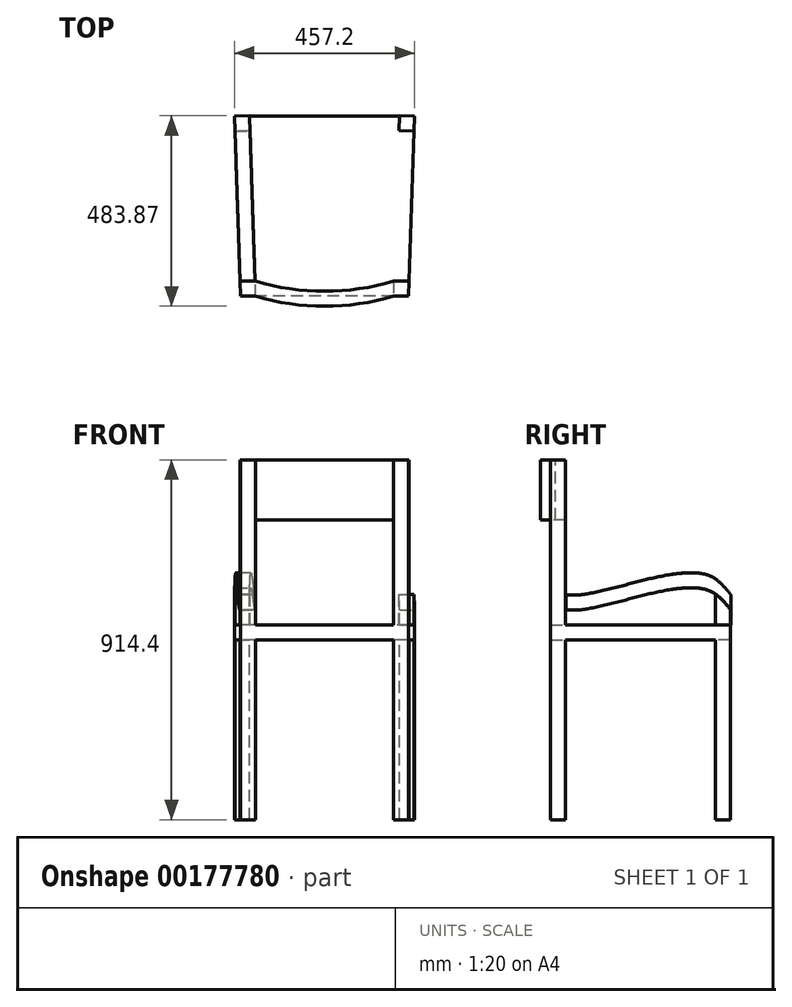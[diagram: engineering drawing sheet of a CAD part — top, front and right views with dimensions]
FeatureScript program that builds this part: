
annotation { "Feature Type Name" : "Feature", "Feature Type Description" : "" }
export const myFeature = defineFeature(function(context is Context, id is Id, definition is map)
    precondition{}
    {
        {
            var Q0;
            Q0=qCreatedBy(makeId("Top.planeOp"),FACE);
            var sketch = newSketch(context, id + "F0", { "sketchPlane" : qUnion([Q0])});
            skLineSegment(sketch, "E0", {"start": v(0, 0) * mm, "end": v(0, 228.6) * mm});
            skLineSegment(sketch, "E1", {"start": v(0, 0) * mm, "end": v(0, -228.6) * mm});
            skLineSegment(sketch, "E2", {"start": v(0, 228.6) * mm, "end": v(228.6, 228.6) * mm});
            skLineSegment(sketch, "E3", {"start": v(0, 228.6) * mm, "end": v(-228.6, 228.6) * mm});
            skLineSegment(sketch, "E4", {"start": v(0, -228.6) * mm, "end": v(-213.36, -228.6) * mm});
            skLineSegment(sketch, "E5", {"start": v(0, -228.6) * mm, "end": v(213.36, -228.6) * mm});
            skLineSegment(sketch, "E6", {"start": v(-228.6, 228.6) * mm, "end": v(-213.36, -228.6) * mm});
            skLineSegment(sketch, "E7", {"start": v(228.6, 228.6) * mm, "end": v(213.36, -228.6) * mm});
            skSolve(sketch);
        }
        {
            var Q0;
            Q0=makeQuery(id+"F0.imprint","IMPRINT",FACE,{"disambiguationData":[TD([[makeQuery(id+"F0.imprint","IMPRINT",EDGE,{"derivedFrom":sQuery(id+"F0.wireOp",EDGE,"E0")}),1.0]])]});
            var Q1;
            Q1=makeQuery(id+"F0.imprint","IMPRINT",FACE,{"disambiguationData":[TD([[makeQuery(id+"F0.imprint","IMPRINT",EDGE,{"derivedFrom":sQuery(id+"F0.wireOp",EDGE,"E0")}),-1.0]])]});
            extrude(context, id + "F1", {"entities" : qUnion([Q0, Q1]), "depth" : 38.1 * mm});
        }
        {
            var Q0;
            Q0=makeQuery(id+"F1.opExtrude","CAP_FACE",FACE,{"disambiguationData":[OSD([sQuery(id+"F0.wireOp",EDGE,"E2"),sQuery(id+"F0.wireOp",EDGE,"E3"),sQuery(id+"F0.wireOp",EDGE,"E4"),sQuery(id+"F0.wireOp",EDGE,"E5"),sQuery(id+"F0.wireOp",EDGE,"E6"),sQuery(id+"F0.wireOp",EDGE,"E7")])],"isStart":true});
            var sketch = newSketch(context, id + "F2", { "sketchPlane" : qUnion([Q0])});
            skLineSegment(sketch, "E8.bottom", {"start": v(228.6, -228.6) * mm, "end": v(190.5, -228.6) * mm});
            skLineSegment(sketch, "E8.top", {"start": v(228.6, -190.5) * mm, "end": v(190.5, -190.5) * mm});
            skLineSegment(sketch, "E8.left", {"start": v(228.6, -228.6) * mm, "end": v(228.6, -190.5) * mm});
            skLineSegment(sketch, "E8.right", {"start": v(190.5, -228.6) * mm, "end": v(190.5, -190.5) * mm});
            skLineSegment(sketch, "E9.bottom", {"start": v(-228.6, -228.6) * mm, "end": v(-190.5, -228.6) * mm});
            skLineSegment(sketch, "E9.top", {"start": v(-228.6, -190.5) * mm, "end": v(-190.5, -190.5) * mm});
            skLineSegment(sketch, "E9.left", {"start": v(-228.6, -228.6) * mm, "end": v(-228.6, -190.5) * mm});
            skLineSegment(sketch, "E9.right", {"start": v(-190.5, -228.6) * mm, "end": v(-190.5, -190.5) * mm});
            skSolve(sketch);
        }
        {
            var Q0;
            {var subQ0=sQuery(id+"F2.wireOp",EDGE,"E8.bottom");Q0=makeQuery(id+"F2.imprint","IMPRINT",FACE,{"disambiguationData":[TD([[makeQuery(id+"F2.imprint","IMPRINT",EDGE,{"derivedFrom":subQ0}),-1.0]])]});}
            var Q1;
            {var subQ0=sQuery(id+"F2.wireOp",EDGE,"E9.bottom");Q1=makeQuery(id+"F2.imprint","IMPRINT",FACE,{"disambiguationData":[TD([[makeQuery(id+"F2.imprint","IMPRINT",EDGE,{"derivedFrom":subQ0}),-1.0]])]});}
            extrude(context, id + "F3", {"entities" : qUnion([Q0, Q1]), "operationType" : NewBodyOperationType.ADD, "depth" : 457.2 * mm});
        }
        {
            var Q0;
            Q0=makeQuery(id+"F1.opExtrude","CAP_FACE",FACE,{"disambiguationData":[OSD([sQuery(id+"F0.wireOp",EDGE,"E2"),sQuery(id+"F0.wireOp",EDGE,"E3"),sQuery(id+"F0.wireOp",EDGE,"E4"),sQuery(id+"F0.wireOp",EDGE,"E5"),sQuery(id+"F0.wireOp",EDGE,"E6"),sQuery(id+"F0.wireOp",EDGE,"E7")])],"isStart":true});
            var sketch = newSketch(context, id + "F4", { "sketchPlane" : qUnion([Q0])});
            skLineSegment(sketch, "E10.bottom", {"start": v(-213.36, 228.6) * mm, "end": v(-175.26, 228.6) * mm});
            skLineSegment(sketch, "E10.top", {"start": v(-213.36, 190.5) * mm, "end": v(-175.26, 190.5) * mm});
            skLineSegment(sketch, "E10.left", {"start": v(-213.36, 228.6) * mm, "end": v(-213.36, 190.5) * mm});
            skLineSegment(sketch, "E10.right", {"start": v(-175.26, 228.6) * mm, "end": v(-175.26, 190.5) * mm});
            skLineSegment(sketch, "E11.bottom", {"start": v(213.36, 228.6) * mm, "end": v(175.26, 228.6) * mm});
            skLineSegment(sketch, "E11.top", {"start": v(213.36, 190.5) * mm, "end": v(175.26, 190.5) * mm});
            skLineSegment(sketch, "E11.left", {"start": v(213.36, 228.6) * mm, "end": v(213.36, 190.5) * mm});
            skLineSegment(sketch, "E11.right", {"start": v(175.26, 228.6) * mm, "end": v(175.26, 190.5) * mm});
            skLineSegment(sketch, "E12", {"start": v(-213.36, 190.5) * mm, "end": v(-214.63, 190.5) * mm});
            skLineSegment(sketch, "E13", {"start": v(213.36, 190.5) * mm, "end": v(214.63, 190.5) * mm});
            skSolve(sketch);
        }
        {
            var Q0;
            {var subQ0=sQuery(id+"F4.wireOp",EDGE,"E10.left");Q0=makeQuery(id+"F4.imprint","IMPRINT",FACE,{"disambiguationData":[TD([[makeQuery(id+"F4.imprint","IMPRINT",EDGE,{"derivedFrom":subQ0}),-1.0]])]});}
            var Q1;
            Q1=makeQuery(id+"F4.imprint","IMPRINT",FACE,{"disambiguationData":[TD([[makeQuery(id+"F4.imprint","IMPRINT",EDGE,{"derivedFrom":sQuery(id+"F4.wireOp",EDGE,"E10.bottom")}),1.0]])]});
            var Q2;
            Q2=makeQuery(id+"F4.imprint","IMPRINT",FACE,{"disambiguationData":[TD([[makeQuery(id+"F4.imprint","IMPRINT",EDGE,{"derivedFrom":sQuery(id+"F4.wireOp",EDGE,"E11.bottom")}),1.0]])]});
            var Q3;
            {var subQ0=sQuery(id+"F4.wireOp",EDGE,"E11.left");Q3=makeQuery(id+"F4.imprint","IMPRINT",FACE,{"disambiguationData":[TD([[makeQuery(id+"F4.imprint","IMPRINT",EDGE,{"derivedFrom":subQ0}),1.0]])]});}
            extrude(context, id + "F5", {"entities" : qUnion([Q0, Q1, Q2, Q3]), "operationType" : NewBodyOperationType.ADD, "endBound" : BoundingType.SYMMETRIC, "depth" : 914.4 * mm});
        }
        {
            var Q0;
            {var subQ0=sQuery(id+"F0.wireOp",EDGE,"E7");Q0=makeQuery(id+"F5.boolean.opBoolean","MERGE",FACE,{"derivedFrom":[makeQuery(id+"F3.boolean.opBoolean","MERGE",FACE,{"derivedFrom":[makeQuery(id+"F1.opExtrude","SWEPT_FACE",FACE,{"disambiguationData":[OSD([subQ0])]}),makeQuery(id+"F3.opExtrude","SWEPT_FACE",FACE,{"disambiguationData":[OSD([subQ0])]})]}),makeQuery(id+"F5.opExtrude","SWEPT_FACE",FACE,{"disambiguationData":[OSD([subQ0])]})]});}
            var sketch = newSketch(context, id + "F6", { "sketchPlane" : qUnion([Q0])});
            skLineSegment(sketch, "E14", {"start": v(236.09, 38.1) * mm, "end": v(236.09, 114.3) * mm});
            skFitSpline(sketch, "E15", {"points": [v(236.09, 114.3) * mm, v(177.93, 164.06) * mm, v(83.5, 165.6) * mm, v(-29.43, 139.8) * mm, v(-144.68, 114.3) * mm, v(-183.24, 114.3) * mm, v(-183.24, 114.3) * mm, v(-183.24, 114.3) * mm], "startDerivative": vector(-272.8, 321.3) * mm, "endDerivative": vector(-246.74, 20.72) * mm});
            skLineSegment(sketch, "E16", {"start": v(-144.68, 114.3) * mm, "end": v(-144.68, 76.2) * mm});
            skLineSegment(sketch, "E17", {"start": v(-29.43, 139.8) * mm, "end": v(-29.43, 101.7) * mm});
            skLineSegment(sketch, "E18", {"start": v(83.5, 165.6) * mm, "end": v(83.5, 127.5) * mm});
            skLineSegment(sketch, "E19", {"start": v(177.93, 164.06) * mm, "end": v(177.93, 125.96) * mm});
            skLineSegment(sketch, "E20", {"start": v(218.9, 134.53) * mm, "end": v(218.9, 96.43) * mm});
            skFitSpline(sketch, "E21", {"points": [v(236.09, 76.2) * mm, v(218.9, 96.43) * mm, v(177.93, 125.96) * mm, v(83.5, 127.5) * mm, v(-29.43, 101.7) * mm, v(-144.68, 76.2) * mm, v(-183.24, 76.2) * mm], "startDerivative": vector(-148.73, 184.43) * mm, "endDerivative": vector(-265.3, 22.13) * mm});
            skLineSegment(sketch, "E22", {"start": v(236.09, 38.1) * mm, "end": v(197.99, 38.1) * mm});
            skLineSegment(sketch, "E23", {"start": v(197.99, 38.1) * mm, "end": v(197.99, 115.42) * mm});
            skSolve(sketch);
        }
        {
            var Q0;
            {var subQ6=sQuery(id+"F6.wireOp",EDGE,"E16");Q0=makeQuery(id+"F6.imprint","IMPRINT",FACE,{"disambiguationData":[TD([[makeQuery(id+"F6.imprint","IMPRINT",EDGE,{"derivedFrom":subQ6}),-1.0]])]});}
            var Q1;
            {var subQ0=sQuery(id+"F6.wireOp",EDGE,"E16");Q1=makeQuery(id+"F6.imprint","IMPRINT",FACE,{"disambiguationData":[TD([[makeQuery(id+"F6.imprint","IMPRINT",EDGE,{"derivedFrom":subQ0}),1.0]])]});}
            var Q2;
            {var subQ0=sQuery(id+"F6.wireOp",EDGE,"E17");Q2=makeQuery(id+"F6.imprint","IMPRINT",FACE,{"disambiguationData":[TD([[makeQuery(id+"F6.imprint","IMPRINT",EDGE,{"derivedFrom":subQ0}),1.0]])]});}
            var Q3;
            {var subQ0=sQuery(id+"F6.wireOp",EDGE,"E18");Q3=makeQuery(id+"F6.imprint","IMPRINT",FACE,{"disambiguationData":[TD([[makeQuery(id+"F6.imprint","IMPRINT",EDGE,{"derivedFrom":subQ0}),1.0]])]});}
            var Q4;
            {var subQ6=sQuery(id+"F6.wireOp",EDGE,"E19");Q4=makeQuery(id+"F6.imprint","IMPRINT",FACE,{"disambiguationData":[TD([[makeQuery(id+"F6.imprint","IMPRINT",EDGE,{"derivedFrom":subQ6}),1.0]])]});}
            var Q5;
            {var subQ0=sQuery(id+"F6.wireOp",EDGE,"E15");var subQ1=sQuery(id+"F6.wireOp",EDGE,"E14");var subQ2=makeQuery(id+"F6.imprint","INTERSECT",VERTEX,{"derivedFrom":[subQ1,subQ0]});Q5=makeQuery(id+"F6.imprint","IMPRINT",FACE,{"disambiguationData":[TD([[makeQuery(id+"F6.imprint","IMPRINT",EDGE,{"disambiguationData":[TD([[subQ2,1.0]])],"derivedFrom":subQ1}),1.0]])]});}
            var Q6;
            {var subQ4=sQuery(id+"F6.wireOp",EDGE,"E22");Q6=makeQuery(id+"F6.imprint","IMPRINT",FACE,{"disambiguationData":[TD([[makeQuery(id+"F6.imprint","IMPRINT",EDGE,{"derivedFrom":subQ4}),-1.0]])]});}
            extrude(context, id + "F7", {"entities" : qUnion([Q0, Q1, Q2, Q3, Q4, Q5, Q6]), "oppositeDirection" : true, "depth" : 38.1 * mm});
        }
        {
            var Q0;
            {var subQ0=sQuery(id+"F0.wireOp",EDGE,"E6");Q0=makeQuery(id+"F5.boolean.opBoolean","MERGE",FACE,{"derivedFrom":[makeQuery(id+"F3.boolean.opBoolean","MERGE",FACE,{"derivedFrom":[makeQuery(id+"F1.opExtrude","SWEPT_FACE",FACE,{"disambiguationData":[OSD([subQ0])]}),makeQuery(id+"F3.opExtrude","SWEPT_FACE",FACE,{"disambiguationData":[OSD([subQ0])]})]}),makeQuery(id+"F5.opExtrude","SWEPT_FACE",FACE,{"disambiguationData":[OSD([subQ0])]})]});}
            var sketch = newSketch(context, id + "F8", { "sketchPlane" : qUnion([Q0])});
            skLineSegment(sketch, "E24", {"start": v(-236.09, 38.1) * mm, "end": v(-236.09, 114.3) * mm});
            skLineSegment(sketch, "E25", {"start": v(-236.09, 38.1) * mm, "end": v(-218.92, 38.1) * mm});
            skLineSegment(sketch, "E26", {"start": v(-236.09, 38.1) * mm, "end": v(-197.99, 38.1) * mm});
            skLineSegment(sketch, "E27", {"start": v(-197.99, 38.1) * mm, "end": v(-177.92, 38.1) * mm});
            skLineSegment(sketch, "E28", {"start": v(-177.92, 38.1) * mm, "end": v(-83.49, 38.1) * mm});
            skLineSegment(sketch, "E29", {"start": v(-83.49, 38.1) * mm, "end": v(29.44, 38.1) * mm});
            skLineSegment(sketch, "E30", {"start": v(29.44, 38.1) * mm, "end": v(144.68, 38.1) * mm});
            skLineSegment(sketch, "E31", {"start": v(144.68, 38.1) * mm, "end": v(144.68, 76.2) * mm});
            skLineSegment(sketch, "E32", {"start": v(29.44, 38.1) * mm, "end": v(29.44, 101.7) * mm});
            skLineSegment(sketch, "E33", {"start": v(-83.49, 38.1) * mm, "end": v(-83.49, 127.5) * mm});
            skLineSegment(sketch, "E34", {"start": v(-177.92, 38.1) * mm, "end": v(-177.92, 125.96) * mm});
            skLineSegment(sketch, "E35", {"start": v(-197.99, 38.1) * mm, "end": v(-197.99, 114.3) * mm});
            skLineSegment(sketch, "E36", {"start": v(-218.92, 38.1) * mm, "end": v(-218.92, 96.44) * mm});
            skLineSegment(sketch, "E37", {"start": v(144.68, 38.1) * mm, "end": v(183.24, 38.1) * mm});
            skLineSegment(sketch, "E38", {"start": v(183.24, 38.1) * mm, "end": v(183.24, 76.2) * mm});
            skLineSegment(sketch, "E39", {"start": v(-236.09, 38.1) * mm, "end": v(-236.09, 76.2) * mm});
            skFitSpline(sketch, "E40", {"points": [v(-236.09, 76.2) * mm, v(-218.92, 96.44) * mm, v(-177.92, 125.96) * mm, v(-83.49, 127.5) * mm, v(29.44, 101.7) * mm, v(144.68, 76.2) * mm, v(183.24, 76.2) * mm], "startDerivative": vector(148.57, 184.57) * mm, "endDerivative": vector(265.28, 22.14) * mm});
            skLineSegment(sketch, "E41", {"start": v(183.24, 76.2) * mm, "end": v(183.24, 114.3) * mm});
            skLineSegment(sketch, "E42", {"start": v(144.68, 76.2) * mm, "end": v(144.68, 114.3) * mm});
            skLineSegment(sketch, "E43", {"start": v(29.44, 101.7) * mm, "end": v(29.44, 139.8) * mm});
            skLineSegment(sketch, "E44", {"start": v(-83.49, 127.5) * mm, "end": v(-83.49, 165.6) * mm});
            skLineSegment(sketch, "E45", {"start": v(-177.92, 125.96) * mm, "end": v(-177.92, 164.06) * mm});
            skLineSegment(sketch, "E46", {"start": v(-218.92, 96.44) * mm, "end": v(-218.92, 134.54) * mm});
            skFitSpline(sketch, "E47", {"points": [v(-236.09, 114.3) * mm, v(-218.92, 134.54) * mm, v(-177.92, 164.06) * mm, v(-83.49, 165.6) * mm, v(29.44, 139.8) * mm, v(144.68, 114.3) * mm, v(183.24, 114.3) * mm], "startDerivative": vector(148.57, 184.57) * mm, "endDerivative": vector(265.28, 22.14) * mm});
            skLineSegment(sketch, "E48", {"start": v(-197.99, 114.3) * mm, "end": v(-197.99, 115.42) * mm});
            skSolve(sketch);
        }
        {
            var Q0;
            {var subQ3=sQuery(id+"F8.wireOp",EDGE,"E36");Q0=makeQuery(id+"F8.imprint","IMPRINT",FACE,{"disambiguationData":[TD([[makeQuery(id+"F8.imprint","IMPRINT",EDGE,{"derivedFrom":subQ3}),1.0]])]});}
            var Q1;
            {var subQ3=sQuery(id+"F8.wireOp",EDGE,"E35");Q1=makeQuery(id+"F8.imprint","IMPRINT",FACE,{"disambiguationData":[TD([[makeQuery(id+"F8.imprint","IMPRINT",EDGE,{"derivedFrom":subQ3}),1.0]])]});}
            var Q2;
            {var subQ1=sQuery(id+"F8.wireOp",EDGE,"E45");Q2=makeQuery(id+"F8.imprint","IMPRINT",FACE,{"disambiguationData":[TD([[makeQuery(id+"F8.imprint","IMPRINT",EDGE,{"derivedFrom":subQ1}),1.0]])]});}
            var Q3;
            {var subQ0=sQuery(id+"F8.wireOp",EDGE,"E44");Q3=makeQuery(id+"F8.imprint","IMPRINT",FACE,{"disambiguationData":[TD([[makeQuery(id+"F8.imprint","IMPRINT",EDGE,{"derivedFrom":subQ0}),1.0]])]});}
            var Q4;
            {var subQ0=sQuery(id+"F8.wireOp",EDGE,"E24");Q4=makeQuery(id+"F8.imprint","IMPRINT",FACE,{"disambiguationData":[TD([[makeQuery(id+"F8.imprint","IMPRINT",EDGE,{"derivedFrom":subQ0}),-1.0]])]});}
            var Q5;
            {var subQ0=sQuery(id+"F8.wireOp",EDGE,"E43");Q5=makeQuery(id+"F8.imprint","IMPRINT",FACE,{"disambiguationData":[TD([[makeQuery(id+"F8.imprint","IMPRINT",EDGE,{"derivedFrom":subQ0}),1.0]])]});}
            var Q6;
            {var subQ0=sQuery(id+"F8.wireOp",EDGE,"E42");Q6=makeQuery(id+"F8.imprint","IMPRINT",FACE,{"disambiguationData":[TD([[makeQuery(id+"F8.imprint","IMPRINT",EDGE,{"derivedFrom":subQ0}),1.0]])]});}
            var Q7;
            {var subQ2=sQuery(id+"F8.wireOp",EDGE,"E41");Q7=makeQuery(id+"F8.imprint","IMPRINT",FACE,{"disambiguationData":[TD([[makeQuery(id+"F8.imprint","IMPRINT",EDGE,{"derivedFrom":subQ2}),1.0]])]});}
            extrude(context, id + "F9", {"entities" : qUnion([Q0, Q1, Q2, Q3, Q4, Q5, Q6, Q7]), "oppositeDirection" : true, "depth" : 38.1 * mm});
        }
        {
            var Q0;
            Q0=makeQuery(id+"F5.opExtrude","CAP_FACE",FACE,{"disambiguationData":[OSD([sQuery(id+"F0.wireOp",EDGE,"E6"),sQuery(id+"F4.wireOp",EDGE,"E10.bottom"),sQuery(id+"F4.wireOp",EDGE,"E10.top"),sQuery(id+"F4.wireOp",EDGE,"E10.right"),sQuery(id+"F4.wireOp",EDGE,"E12")])],"isStart":true});
            var sketch = newSketch(context, id + "F10", { "sketchPlane" : qUnion([Q0])});
            skLineSegment(sketch, "E49", {"start": v(-175.26, -190.5) * mm, "end": v(175.26, -190.5) * mm});
            skLineSegment(sketch, "E50", {"start": v(0, -190.5) * mm, "end": v(0, -215.9) * mm});
            skPoint(sketch, "E50.endSnap0", {"position": v(0, -190.5) * mm});
            skArc(sketch, "E51", {"start": v(-175.26, -190.5) * mm, "mid": v(0, -215.9) * mm, "end": v(175.26, -190.5) * mm});
            skLineSegment(sketch, "E52", {"start": v(0, -215.9) * mm, "end": v(0, -254) * mm});
            skLineSegment(sketch, "E53", {"start": v(-175.26, -228.6) * mm, "end": v(175.26, -228.6) * mm});
            skArc(sketch, "E54", {"start": v(-175.26, -228.6) * mm, "mid": v(0, -254) * mm, "end": v(175.26, -228.6) * mm});
            skLineSegment(sketch, "E55", {"start": v(175.26, -190.5) * mm, "end": v(175.26, -228.6) * mm});
            skSolve(sketch);
        }
        {
            var Q0;
            {var subQ0=sQuery(id+"F10.wireOp",EDGE,"E54");var subQ1=sQuery(id+"F10.wireOp",EDGE,"E52");var subQ2=makeQuery(id+"F10.imprint","INTERSECT",VERTEX,{"derivedFrom":[subQ1,subQ0]});Q0=makeQuery(id+"F10.imprint","IMPRINT",FACE,{"disambiguationData":[TD([[makeQuery(id+"F10.imprint","IMPRINT",EDGE,{"disambiguationData":[TD([[subQ2,1.0]])],"derivedFrom":subQ1}),1.0]])]});}
            var Q1;
            {var subQ0=sQuery(id+"F10.wireOp",EDGE,"E54");var subQ1=sQuery(id+"F10.wireOp",EDGE,"E52");var subQ2=makeQuery(id+"F10.imprint","INTERSECT",VERTEX,{"derivedFrom":[subQ1,subQ0]});Q1=makeQuery(id+"F10.imprint","IMPRINT",FACE,{"disambiguationData":[TD([[makeQuery(id+"F10.imprint","IMPRINT",EDGE,{"disambiguationData":[TD([[subQ2,1.0]])],"derivedFrom":subQ1}),-1.0]])]});}
            var Q2;
            {var subQ1=makeQuery(id+"F5.opExtrude","CAP_EDGE",EDGE,{"disambiguationData":[OSD([sQuery(id+"F4.wireOp",EDGE,"E10.right")])],"isStart":true});Q2=makeQuery(id+"F10.imprint","IMPRINT",FACE,{"disambiguationData":[TD([[makeQuery(id+"F10.imprint","IMPRINT",EDGE,{"derivedFrom":subQ1}),-1.0]])]});}
            var Q3;
            {var subQ0=sQuery(id+"F10.wireOp",EDGE,"E55");Q3=makeQuery(id+"F10.imprint","IMPRINT",FACE,{"disambiguationData":[TD([[makeQuery(id+"F10.imprint","IMPRINT",EDGE,{"derivedFrom":subQ0}),-1.0]])]});}
            extrude(context, id + "F11", {"entities" : qUnion([Q0, Q1, Q2, Q3]), "operationType" : NewBodyOperationType.ADD, "oppositeDirection" : true, "depth" : 152.4 * mm});
        }
    });
